# Revit family: PRD_AR_WshbsnTps_F5LME-HybridWashbasinTap_F5LME005 2
name_source: partatom
category: Plumbing Fixtures
units: mm (PartAtom-declared; Revit-internal decimal feet)

## family parameters
Always vertical = Yes
Cut with Voids When Loaded = No
Enable Cutting in Views = No
Maintain Annotation Orientation = No
OmniClass Number = 23.45.55.17
OmniClass Title = Mixing Faucets
Part Type = Normal
Room Calculation Point = No
Round Connector Dimension = Use Diameter
Shared = No
Work Plane-Based = No

## types (1)
- F5LME005
    AccentColour = none
    AssetType = Fixed
    BIMObjectName = PRD_AR_WashbasinTaps_F5LME-HybridWashbasinTap_F5LME005
    BodyMaterial = PRD_AR_StainlessSteel_Brushed
    Category = Pr_40_20_87_98, Washbasin taps
    Default Elevation = 0 mm  [stored 0 ft]
    Depressurised = no
    Description = F5LME hybrid washbasin tap DN 15 as pillar mixer with swivelling spout, can be locked in the centre position. Adjustable swivel ranges of 50°, 120° and 360°. For connection to hot water and cold water via hoses with strainers. Single lever mixer with mixer cartridge with ceramic disc technology and adjustable, turn-proof temperature stop. Alternative activation using hand reflection via an opto-electronic sensor for time-controlled water release with preset mixing water temperature. Mixer cartridge, solenoid valve and sensor with control electronics in all-metal housing, brushed stainless steel. Laminar jet controller with integrated flow rate controller (8.0 l/min). Projection 220 mm. Activated water hygiene flushing 24 hours after last activation, safety switch-off for continuous reflection and saving of statistical data. With option for parametrisation and communication via optional, bidirectional remote control. Optionally for battery operation with battery compartment including 6 V lithium battery (CR-P2) per fitting for installation under the kitchen sink or for separate power supply via 6.75 V/12 V DC power supply unit or AQUA 3000 open system accessories.
    DiameterNominal = DN 15
    Export Type to IFC As = IfcValveType
    FaucetFunction = MIXED
    FaucetOperation = LEVERHANDLE
    FaucetType = PILLAR
    Features = For connection to hot water and cold water via hoses with strainers. Projection 220 mm. Battery compartment including battery or power supply unit with extension cable must be ordered separately.
    Finish = brushed
    FlowColdWater = 0.0 L/s
    FlowHotWater = 0.0 L/s
    FunctionalPrinciple = manual
    HygieneFlushing = prepared
    IfcExportAs = IfcValveType
    IfcExportType = FAUCET
    InletConversionSize = 10 mm
    InletSize = G3/8
    LockingMechanism = Top section, non-ceramic
    Manufacturer = KWC Group Management AG
    ManufacturerName = KWC Group Management AG
    ManufacturerURL = www.kwc-professional.com
    Material = stainless steel
    MaterialFitting = stainless steel
    MinimumFlowPressure = 1 bar
    Model = F5LME005
    ModelNumber = 3600008404
    ModelReference = F5LME005
    NBSDescription = Water supply fittings for wash basins and troughs
    NBSReference = 45-35-70/371
    Name = F5LME Hybrid washbasin tap F5LME005
    NominalDepth = 0 mm  [stored 0 ft]
    NominalHeight = 292 mm  [stored 0.958005 ft]
    NominalLength = 0 mm  [stored 0 ft]
    NominalWidth = 0 mm  [stored 0 ft]
    Pop-UpWasteSet = no
    ProductInformation = http://pim.kwc.com
    Spout = rotating, top
    SpoutProjection = 175 mm
    SurfaceFinishFitting = brushed
    TemperatureLimit = yes
    ThermalDisinfection = yes
    Type IFC Predefined Type = FAUCET
    TypeOfMixing = yes
    TypeOfMounting = tap hole
    TypeOfOperation = manual operation
    TypeOfTap = pillar tap
    URL = www.kwc-professional.com
    Uniclass2015Code = Pr_40_20_87_98
    Uniclass2015Title = Washbasin taps
    Uniclass2015Version = Products v1.38
    Version = 1
    VolumeFlowRateAt3Bar = 0.13 l/s
    WaterConnection = hose (gland nut)
    WithFilter = yes
    WithRosettes/CoverPlate = no

note: [stored X ft] marks values corroborated as IEEE doubles in the binary element streams (Revit-internal decimal feet)

## geometry (parser evidence)
native form markers: Sweep x6
no freeform markers — native parametric forms only
